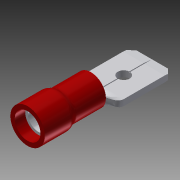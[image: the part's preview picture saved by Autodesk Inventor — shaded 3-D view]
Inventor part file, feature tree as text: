
AUTODESK INVENTOR PART (.ipt)
format: ipt  version: 2014 (Build 180170000, 170)  size: 363,008 bytes
history: native  units: in
note: dims shown in document units (in); Inventor stores cm internally (conversion verified against a paired STEP export)
features: sketch x8, extrude x6, projected_geometry x6, chamfer x4, fillet x2, shell x1, revolve x1, plane x1, loft x1, other x1
ambient origin geometry x8: Origin, YZ Plane, XZ Plane, XY Plane, X Axis, Y Axis, Z Axis, Center Point
bodies: Solid1 (feature_tree), Solid2 (feature_tree)
feature tree (31):
  extrude  "Extrusion1"  Depth=0.378in TaperAngle=0.0deg
  extrude  "Extrusion2"  Depth=0.171in TaperAngle=0.0deg
  fillet  "Fillet1"  Radius=0.05in
  shell  "Shell1"  Thickness=0.026in
  revolve  "Revolution1"  [1 undecoded]
  plane  "Work Plane1"
  extrude  "Extrusion3"  Depth=0.02in
  loft  "Loft1"
  fillet  "Fillet3"  Radius=0.036in
  chamfer  "Chamfer1"  Angle=90.0deg  [1 undecoded]
  extrude  "Extrusion4"  Depth=0.005in TaperAngle=45.0deg
  chamfer  "Chamfer2"  Distance=0.005in Angle=45.0deg
  chamfer  "Chamfer3"  Distance=0.03in Angle=45.0deg
  chamfer  "Chamfer4"  Distance=1.0in
  extrude  "Extrusion5"  Depth=0.005in
  extrude  "Extrusion6"  Depth=0.005in TaperAngle=0.0deg
  sketch  "Sketch1"  dims[d0=0.1795in d1=0.378in d2=0.0in]
  sketch  "Sketch2"  dims[d3=0.2055in d4=0.171in d5=0.0in d6=0.05in d7=0.026in]
  projected_geometry  "Projected Loop1"
  sketch  "Sketch3"  dims[d11=90.0deg d12=-0.06in]
  sketch  "Sketch4"  dims[d17=0.036in d18=0.0in d24=0.02in]
  sketch  "Sketch5"  dims[d27=0.003in d28=0.125in d29=45.0deg d30=0.005in d31=0.036in d32=0.0in]
  projected_geometry  "Projected Loop2"
  sketch  "Sketch6"  dims[d33=0.248in d36=0.0in d37=90.0deg]
  other  "Edges2"
  sketch  "Sketch7"  dims[d38=0.3937in d39=90.0deg d40=0.05in d41=0.005in d42=45.0deg d43=0.005in d44=0.05in d45=45.0deg d46=0.03in d47=0.05in d48=45.0deg]
  projected_geometry  "Projected Loop3"
  sketch  "Sketch8"  dims[d49=0.0715in d50=1.0in d51=0.0in d52=0.005in d53=0.005in d54=0.0in d55=0.0135in d56=0.2925in d57=0.075in]
  projected_geometry  "Projected Loop4"
  projected_geometry  "Project Cut Edges1"
  projected_geometry  "Project Cut Edges2"
note: 2 required parameter values undecoded (feature->parameter linkage not recoverable at this tier; creation-order binding heuristic only, values carry confidence <= 0.55)